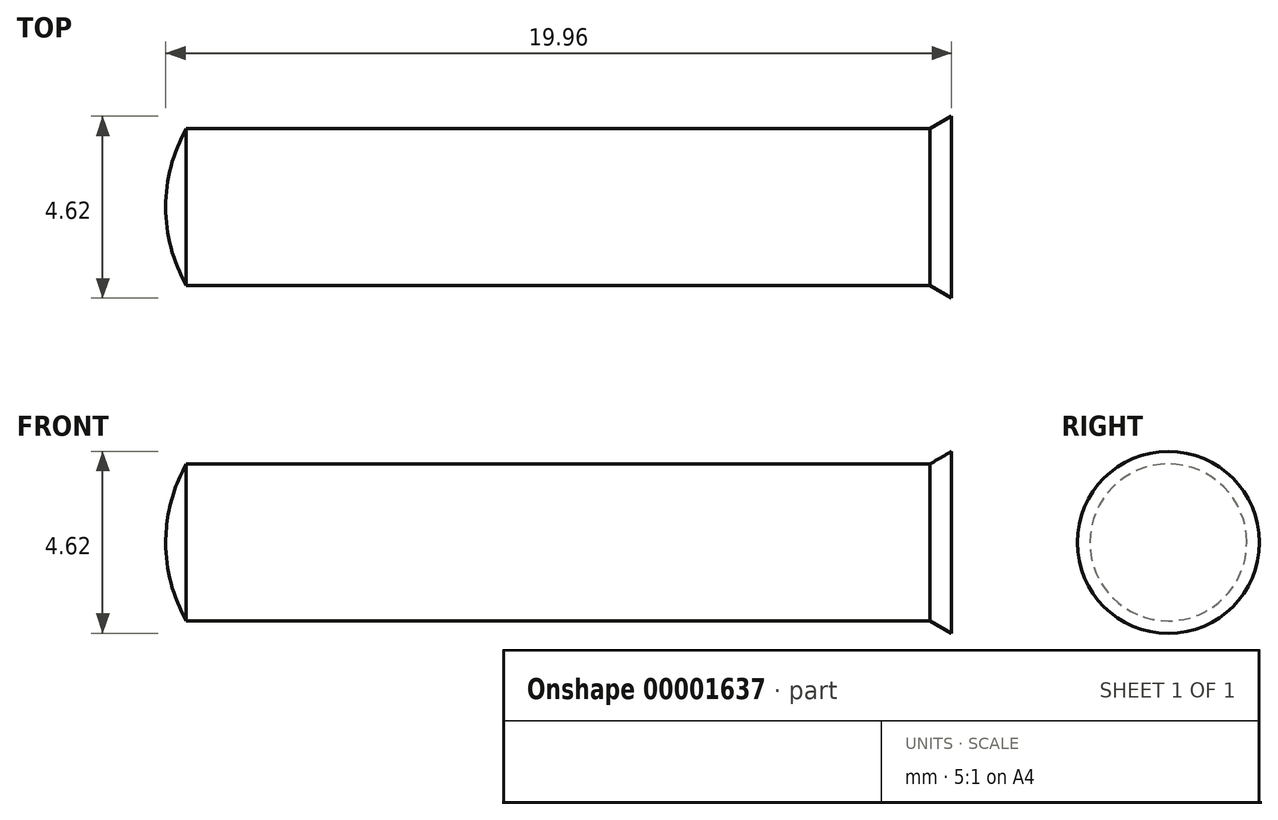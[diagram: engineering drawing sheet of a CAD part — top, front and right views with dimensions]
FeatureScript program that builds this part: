
annotation { "Feature Type Name" : "Feature", "Feature Type Description" : "" }
export const myFeature = defineFeature(function(context is Context, id is Id, definition is map)
    precondition{}
    {
        {
            var Q0;
            Q0=qCreatedBy(makeId("Front.planeOp"),FACE);
            var sketch = newSketch(context, id + "F0", { "sketchPlane" : qUnion([Q0])});
            skLineSegment(sketch, "E0", {"start": v(0, 0) * mm, "end": v(19.96, 0) * mm});
            skLineSegment(sketch, "E1", {"start": v(19.96, 0) * mm, "end": v(19.96, 2.31) * mm});
            skLineSegment(sketch, "E2", {"start": v(19.96, 2.31) * mm, "end": v(19.41, 2) * mm});
            skLineSegment(sketch, "E3", {"start": v(19.41, 2) * mm, "end": v(0.52, 2) * mm});
            skArc(sketch, "E4", {"start": v(0.52, 2) * mm, "mid": v(0.13, 1.03) * mm, "end": v(0, 0) * mm});
            skSolve(sketch);
        }
        {
            var Q0;
            Q0=makeQuery(id+"F0.imprint","IMPRINT",FACE,{"disambiguationData":[TD([[makeQuery(id+"F0.imprint","IMPRINT",EDGE,{"derivedFrom":sQuery(id+"F0.wireOp",EDGE,"E0")}),1.0]])]});
            var Q1;
            Q1=sQuery(id+"F0.wireOp",EDGE,"E0");
            revolve(context, id + "F1", {"entities" : qUnion([Q0]), "axis" : qUnion([Q1]), "revolveType" : RevolveType.FULL});
        }
    });
